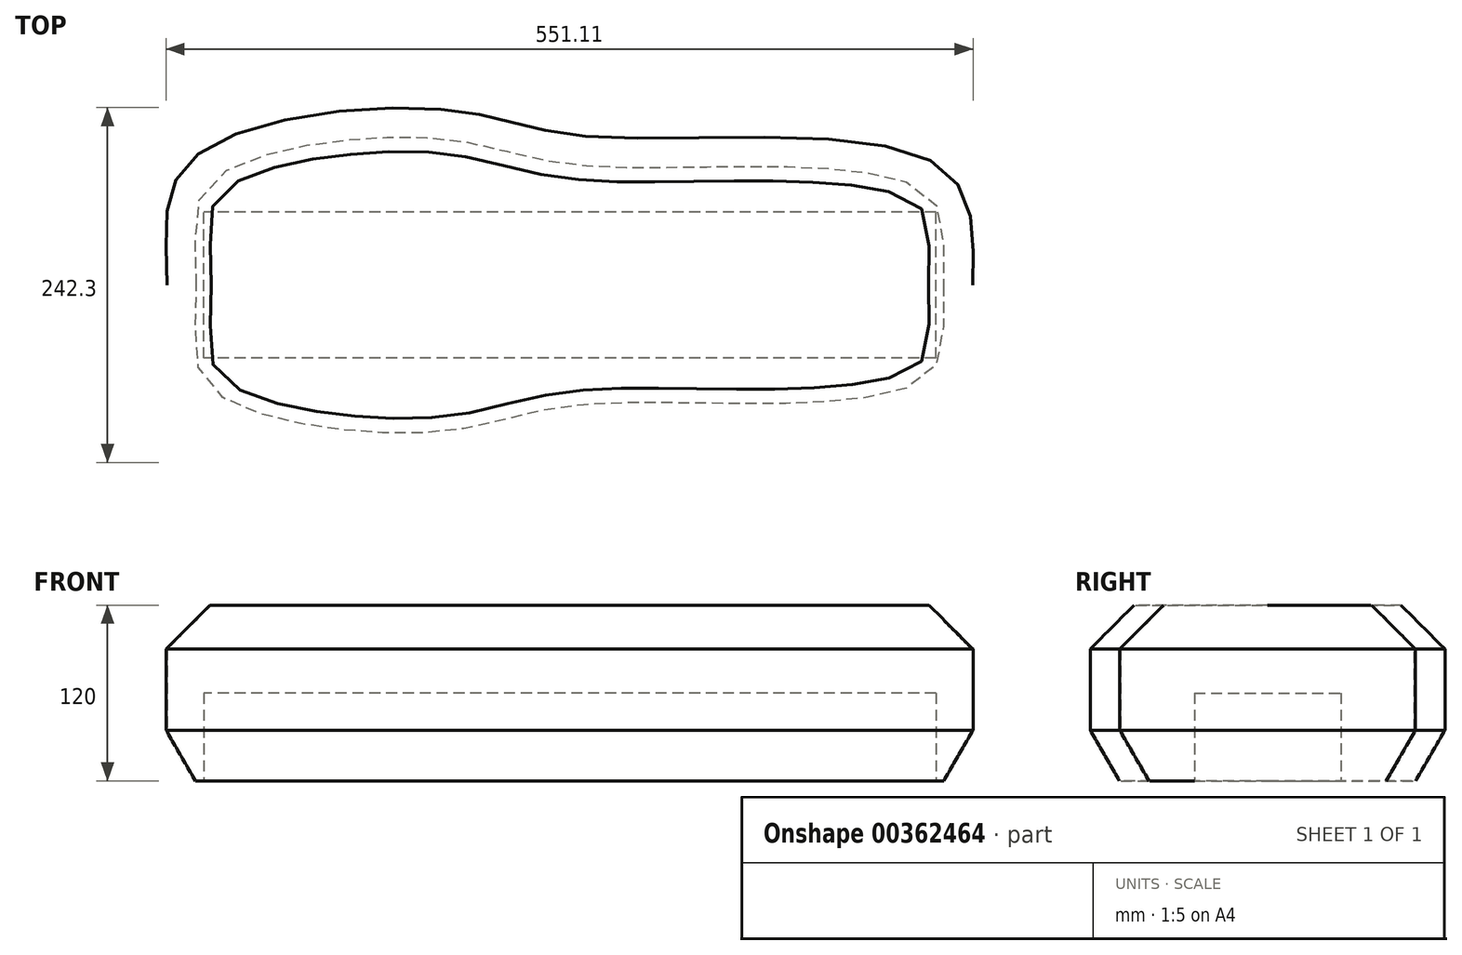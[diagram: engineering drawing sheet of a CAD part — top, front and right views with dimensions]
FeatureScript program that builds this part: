
annotation { "Feature Type Name" : "Feature", "Feature Type Description" : "" }
export const myFeature = defineFeature(function(context is Context, id is Id, definition is map)
    precondition{}
    {
        {
            var Q0;
            Q0=qCreatedBy(makeId("Top.planeOp"),FACE);
            var sketch = newSketch(context, id + "F0", { "sketchPlane" : qUnion([Q0])});
            skFitSpline(sketch, "E0", {"points": [v(0, 0) * mm, v(16.1, 85.47) * mm, v(188.93, 120) * mm, v(289.7, 101.4) * mm, v(529.35, 80) * mm, v(550, 0) * mm], "startDerivative": vector(0, 620.1) * mm, "endDerivative": vector(0, -492.05) * mm});
            skFitSpline(sketch, "E1.MirrorCS", {"points": [v(0, 0) * mm, v(16.1, -85.47) * mm, v(188.93, -120) * mm, v(289.7, -101.4) * mm, v(529.35, -80) * mm, v(550, 0) * mm], "startDerivative": vector(0, -620.1) * mm, "endDerivative": vector(0, 492.05) * mm});
            skSolve(sketch);
        }
        {
            var Q0;
            Q0=makeQuery(id+"F0.imprint","IMPRINT",FACE,{"disambiguationData":[TD([[makeQuery(id+"F0.imprint","IMPRINT",EDGE,{"derivedFrom":sQuery(id+"F0.wireOp",EDGE,"E0")}),-1.0]])]});
            extrude(context, id + "F1", {"entities" : qUnion([Q0]), "depth" : 120 * mm, "offsetDistance" : 25 * mm});
        }
        {
            var Q0;
            Q0=makeQuery(id+"F1.opExtrude","CAP_EDGE",EDGE,{"disambiguationData":[OSD([sQuery(id+"F0.wireOp",EDGE,"E1.MirrorCS")])],"isStart":false});
            chamfer(context, id + "F2", {"entities" : qUnion([Q0]), "width" : 30 * mm, "tangentPropagation" : true});
        }
        {
            var Q0;
            Q0=makeQuery(id+"F1.opExtrude","CAP_FACE",FACE,{"disambiguationData":[OSD([sQuery(id+"F0.wireOp",EDGE,"E0"),sQuery(id+"F0.wireOp",EDGE,"E1.MirrorCS")])],"isStart":true});
            chamfer(context, id + "F3", {"entities" : qUnion([Q0]), "chamferType" : ChamferType.OFFSET_ANGLE, "width" : 20 * mm, "oppositeDirection" : false, "angle" : 60 * degree, "tangentPropagation" : true});
        }
        {
            var Q0;
            Q0=makeQuery(id+"F1.opExtrude","CAP_FACE",FACE,{"disambiguationData":[OSD([sQuery(id+"F0.wireOp",EDGE,"E0"),sQuery(id+"F0.wireOp",EDGE,"E1.MirrorCS")])],"isStart":true});
            var sketch = newSketch(context, id + "F4", { "sketchPlane" : qUnion([Q0])});
            skLineSegment(sketch, "E2.bottom", {"start": v(525, 50) * mm, "end": v(25, 50) * mm});
            skLineSegment(sketch, "E2.top", {"start": v(525, -50) * mm, "end": v(25, -50) * mm});
            skLineSegment(sketch, "E2.left", {"start": v(525, 50) * mm, "end": v(525, -50) * mm});
            skLineSegment(sketch, "E2.right", {"start": v(25, 50) * mm, "end": v(25, -50) * mm});
            skPoint(sketch, "E2.middle", {"position": v(275, 0) * mm});
            skSolve(sketch);
        }
        {
            var Q0;
            Q0 = qSketchRegion(id + "F4", true);
            extrude(context, id + "F5", {"entities" : qUnion([Q0]), "operationType" : NewBodyOperationType.REMOVE, "oppositeDirection" : true, "depth" : 60 * mm, "offsetDistance" : 25 * mm});
        }
    });
